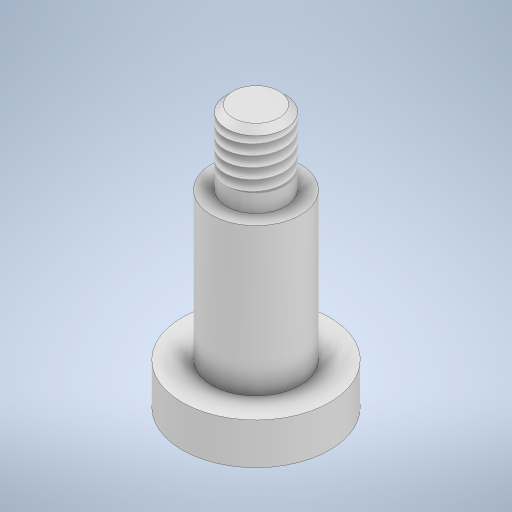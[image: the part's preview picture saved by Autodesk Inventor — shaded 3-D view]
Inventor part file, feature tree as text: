
AUTODESK INVENTOR PART (.ipt)
format: ipt  version: 2024.2 (Build 282272000, 272)  size: 287,744 bytes
history: native  units: mm
features: sketch x2, revolve x1, thread x1, extrude x1, chamfer x1
ambient origin geometry x8: Origin, YZ Plane, XZ Plane, XY Plane, X Axis, Y Axis, Z Axis, Center Point
bodies: Solid1 (feature_tree)
feature tree (6):
  revolve  "Revolution1"  [1 undecoded]
  thread  "Thread1"  [1 undecoded]
  extrude  "Extrusion1"  Depth=10.0mm
  chamfer  "Chamfer1"  Distance=2.8mm
  sketch  "Sketch1"  dims[d0=10.0mm d1=6.0mm d2=4.0mm]
  sketch  "Sketch2"  dims[d3=5.0mm d4=10.0mm d5=2.8mm d6=90.0deg d7=6.0mm d8=1.2mm d9=2.5mm d10=2.0mm d11=0.0mm d12=0.43mm d13=2.0mm d14=45.0deg]
note: 2 required parameter values undecoded (feature->parameter linkage not recoverable at this tier; creation-order binding heuristic only, values carry confidence <= 0.55)